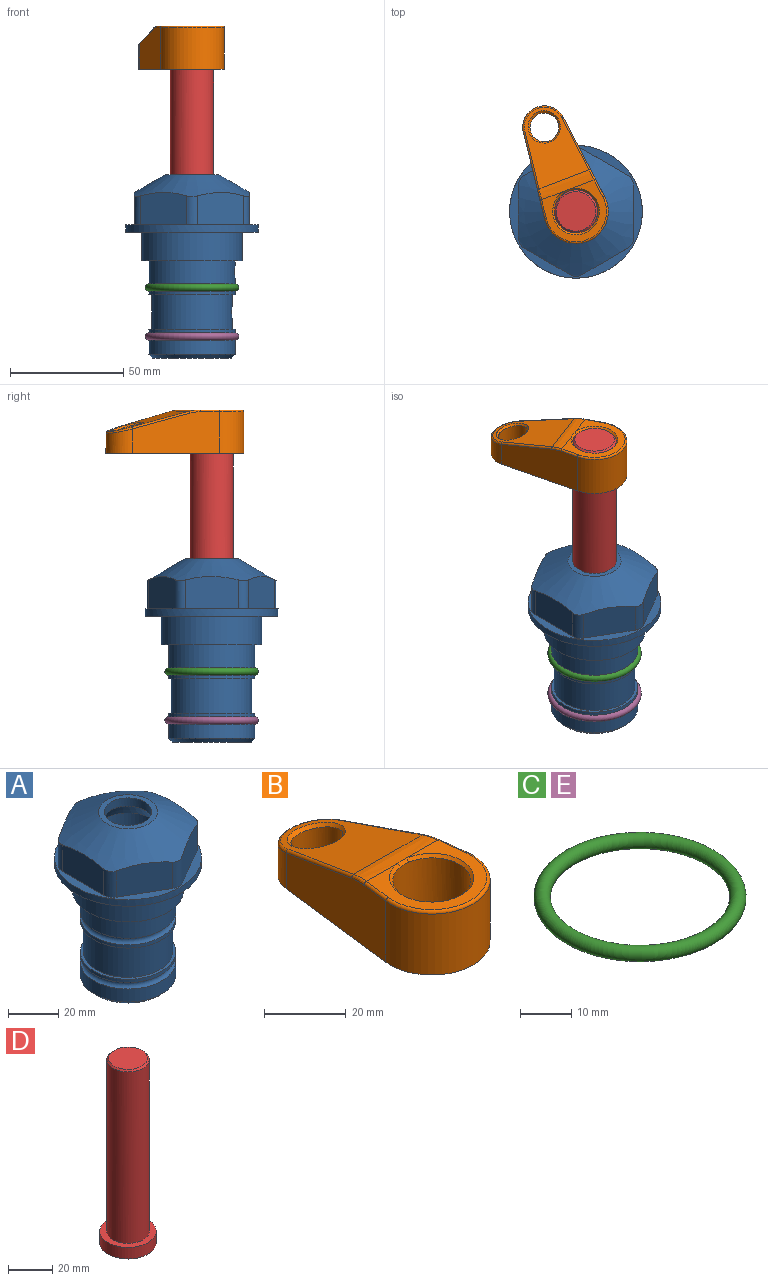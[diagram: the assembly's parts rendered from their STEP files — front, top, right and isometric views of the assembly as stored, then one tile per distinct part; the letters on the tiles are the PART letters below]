
ASSEMBLY  parts=5 mates=4
PART A: 36 faces, bbox 58.7x58.7x81 mm
  f0: cylinder r=17.78mm len=35.56mm, axis (0,0,1), area 1670.8mm2, adj f23,f24,f31
  f1: cylinder r=19.05mm len=38.1mm, axis (0,0,1), area 1191.9mm2, adj f26,f27,f30
  f2: plane 58.66x58.66mm, normal (0,0,-1), area 1150.6mm2, adj f3,f28
  f3: cylinder r=29.33mm len=58.66mm, axis (0,0,-1), area 585.1mm2, adj f2,f4
  f4: plane 58.66x58.66mm, normal (0,0,1), area 475.9mm2, adj f3,f5,f6,f7,f8,f9,f10,f11
  f5: plane 20.32x14.34mm, normal (-0.5,0.87,0), area 324.4mm2, adj f4,f15,f16,f17
  f6: plane 20.32x14.34mm, normal (0.5,0.87,0), area 324.4mm2, adj f4,f14,f15,f17
  f7: plane 23.48x14.34mm, normal (1,0,0), area 324.4mm2, adj f4,f13,f14,f17
  f8: plane 20.32x14.34mm, normal (0.5,-0.87,0), area 324.4mm2, adj f4,f12,f13,f17
  f9: plane 20.32x14.34mm, normal (-0.5,-0.87,0), area 324.4mm2, adj f4,f11,f12,f17
  f10: plane 23.48x14.34mm, normal (-1,0,0), area 324.4mm2, adj f4,f11,f16,f17
  f11: cylinder r=5.08mm len=12.85mm, axis (0,0,-1), area 67.2mm2, adj f4,f9,f10,f17
  f12: cylinder r=5.08mm len=12.85mm, axis (0,0,-1), area 67.2mm2, adj f4,f8,f9,f17
  f13: cylinder r=5.08mm len=12.85mm, axis (0,0,-1), area 67.2mm2, adj f4,f7,f8,f17
  f14: cylinder r=5.08mm len=12.85mm, axis (0,0,-1), area 67.2mm2, adj f4,f6,f7,f17
  f15: cylinder r=5.08mm len=12.85mm, axis (0,0,-1), area 67.2mm2, adj f4,f5,f6,f17
  f16: cylinder r=5.08mm len=12.85mm, axis (0,0,-1), area 67.2mm2, adj f4,f5,f10,f17
  f17: cone r=11.73mm half-angle=60deg, axis (0,0,-1), area 2071.8mm2, adj f5,f6,f7,f8,f9,f10,f11,f12
  f18: plane 23.46x23.46mm, normal (0,0,1), area 147.4mm2, adj f17,f35
  f19: plane 34.93x34.93mm, normal (0,0,-1), area 958mm2, adj f29
  f20: cylinder r=19.05mm len=38.1mm, axis (0,0,1), area 760.1mm2, adj f21,f29
  f21: torus R=19.05mm, axis (0,0,1), area 565.3mm2, adj f20,f22
  f22: cylinder r=19.05mm len=38.1mm, axis (0,0,1), area 190mm2, adj f21,f23
  f23: plane 38.1x38.1mm, normal (0,0,1), area 146.9mm2, adj f0,f22
  f24: plane 38.1x38.1mm, normal (0,0,-1), area 146.9mm2, adj f0,f25
  f25: cylinder r=19.05mm len=38.1mm, axis (0,0,1), area 190mm2, adj f24,f26
  f26: torus R=19.05mm, axis (0,0,1), area 565.3mm2, adj f1,f25
  f27: plane 44.45x44.45mm, normal (0,0,-1), area 411.7mm2, adj f1,f28
  f28: cylinder r=22.23mm len=44.45mm, axis (0,0,1), area 1773.5mm2, adj f2,f27
  f29: cone r=19.05mm half-angle=45deg, axis (0,0,1), area 257.5mm2, adj f19,f20
  f30: cylinder r=3.17mm len=6.75mm, axis (-1,0,0), area 128mm2, adj f1,f33
  f31: cylinder r=3.17mm len=6.35mm, axis (-1,0,0), area 102.5mm2, adj f0,f33
  f32: plane 25.4x25.4mm, normal (0,0,1), area 506.7mm2, adj f33
  f33: cylinder r=12.7mm len=66.42mm, axis (0,0,-1), area 5236.2mm2, adj f30,f31,f32,f34
  f34: cone r=9.53mm half-angle=30deg, axis (0,0,-1), area 443.4mm2, adj f33,f35
  f35: cylinder r=9.53mm len=19.05mm, axis (0,0,-1), area 240.9mm2, adj f18,f34
PART B: 31 faces, bbox 31.7x65.5x19.8 mm
  f0: plane 39.12x18.26mm, normal (0.99,0.12,0), area 612.2mm2, adj f1,f4,f7,f11,f13,f15
  f1: cylinder r=9.53mm len=18.91mm, axis (0,0,-1), area 296.1mm2, adj f0,f2,f7,f17
  f2: plane 39.12x18.26mm, normal (-0.99,0.12,0), area 612.2mm2, adj f1,f4,f7,f12,f14,f16
  f3: cylinder r=6.35mm len=12.7mm, axis (0,0,-1), area 362.4mm2, adj f7,f18
  f4: cylinder r=14.29mm len=28.58mm, axis (0,0,-1), area 882.2mm2, adj f0,f2,f7,f10
  f5: cylinder r=9.53mm len=19.05mm, axis (0,0,-1), area 1092.6mm2, adj f7,f19,f20
  f6: plane 26.99x23.69mm, normal (0,0,1), area 216.2mm2, adj f9,f10,f11,f12,f19
  f7: plane 63.5x28.58mm, normal (0,0,-1), area 661.8mm2, adj f0,f1,f2,f3,f4,f5,f22,f23
  f8: plane 33.52x23.6mm, normal (0,0.26,0.97), area 486mm2, adj f9,f15,f16,f17,f18
  f9: cylinder r=19.05mm len=24.72mm, axis (1,0,0), area 120.4mm2, adj f6,f8,f13,f14,f20
  f10: torus R=13.49mm, axis (0,0,1), area 59mm2, adj f4,f6,f11,f12
  f11: cylinder r=0.79mm len=8.67mm, axis (0.12,-0.99,0), area 10.8mm2, adj f0,f6,f10,f13
  f12: cylinder r=0.79mm len=8.67mm, axis (0.12,0.99,0), area 10.8mm2, adj f2,f6,f10,f14
  f13: bspline ~4.95x1.42mm, area 6.1mm2, adj f0,f9,f11,f15
  f14: bspline ~4.95x1.42mm, area 6.1mm2, adj f2,f9,f12,f16
  f15: cylinder r=0.79mm len=25.95mm, axis (0.12,-0.96,0.26), area 32.9mm2, adj f0,f8,f13,f17
  f16: cylinder r=0.79mm len=25.95mm, axis (0.12,0.96,-0.26), area 32.9mm2, adj f2,f8,f14,f17
  f17: bspline ~18.91x8.38mm, area 30mm2, adj f1,f8,f15,f16
  f18: bspline ~14.29x14.29mm, area 48.3mm2, adj f3,f8
  f19: cone r=9.53mm half-angle=45deg, axis (0,0,1), area 66.5mm2, adj f5,f6,f20
  f20: bspline ~3.22x0.96mm, area 3.5mm2, adj f5,f9,f19
  f21: plane 2.75x2.72mm, normal (0,0,-1), area 2.9mm2, adj f23,f25,f28
  f22: plane 23.05x15.88mm, normal (-0.99,-0.12,0), area 323.6mm2, adj f7,f25,f26,f27,f28,f29
  f23: plane 23.05x15.88mm, normal (0.99,-0.12,0), area 323.6mm2, adj f7,f21,f25,f27,f28,f30
  f24: cylinder r=9.53mm len=10.69mm, axis (0,0,-1), area 114.7mm2, adj f7,f27,f29,f30
  f25: cylinder r=12.7mm len=20.59mm, axis (0,0,-1), area 381.1mm2, adj f7,f21,f22,f23,f26,f28
  f26: plane 2.75x2.72mm, normal (0,0,-1), area 2.9mm2, adj f22,f25,f28
  f27: plane 19.72x18.37mm, normal (0,-0.26,-0.97), area 291.8mm2, adj f22,f23,f24,f28,f29,f30
  f28: cylinder r=15.88mm len=19.92mm, axis (1,0,0), area 54.8mm2, adj f21,f22,f23,f25,f26,f27
  f29: cylinder r=1.59mm len=11mm, axis (0,0,-1), area 34.7mm2, adj f7,f22,f24,f27
  f30: cylinder r=1.59mm len=11mm, axis (0,0,-1), area 34.7mm2, adj f7,f23,f24,f27
PART C: 1 faces, bbox 44.7x44.7x3.2 mm
  f0: torus R=19.05mm, axis (0,0,1), area 1193.9mm2
PART D: 6 faces, bbox 25.4x25.4x101.6 mm
  f0: plane 17.46x17.46mm, normal (0,0,1), area 239.5mm2, adj f5
  f1: plane 25.4x25.4mm, normal (0,0,-1), area 506.7mm2, adj f2
  f2: cylinder r=12.7mm len=25.4mm, axis (0,0,1), area 506.7mm2, adj f1,f3
  f3: plane 25.4x25.4mm, normal (0,0,1), area 221.7mm2, adj f2,f4
  f4: cylinder r=9.53mm len=94.46mm, axis (0,0,1), area 5653mm2, adj f3,f5
  f5: cone r=8.73mm half-angle=45deg, axis (0,0,-1), area 64.4mm2, adj f0,f4
PART E: same geometry as C
PLACE A at identity fixed
PLACE B rot(axis=(0,0,1),20.6deg) t=(0,0,27.55)mm
PLACE C at identity
PLACE D rot(axis=(0,0,1),20.6deg) t=(0,0,27.55)mm
PLACE E t=(0,0,-21.59)mm
MATE fastened C.f0 <-> A.f0  axis (0,0,1) through (0,0,-24.51)mm
MATE cylindrical D.f2 <-> A.f0  axis (0,0,-1) through (0,0,-10.55)mm
MATE fastened D.f2 <-> B.f4  axis (0,0,1) through (0,0,91.05)mm
MATE fastened E.f0 <-> A.f0  axis (0,0,1) through (0,0,-46.1)mm
